# Revit family: STORA-RP 650x
name_source: partatom
category: Leuchten
units: mm (PartAtom-declared; Revit-internal decimal feet)

## family parameters
Basisbauteil = Fläche
Beim Laden mit Abzugskörper schneiden = Nein
Bemaßung runder Anschluss = Durchmesser verwenden
Gemeinsam genutzt = Nein
Lichtquelle = Ja
OmniClass-Nummer = 23.80.70.11
OmniClass-Titel = Luminaries for Internal Lighting
Raumberechnungspunkt = Nein
Teiletyp = Normal

## types (4) — shared parameters
Baugruppenkennzeichen = D5020200
Datei für fotometrisches Netz = STORA-RP_650_OS.IES
Emissionsform beim Rendern sichtbar = Nein
Farbfilter = 16777215
Farbtemperaturverschiebung bei Dämpfen der Lampe = <Keine Auswahl>
Hersteller = RIDI Leuchten GmbH
Lampe = LED
Neigungswinkel = 90.00°
Scheinlast = 37 VA
URL = www.spectral.de
Von Kreisdurchmesser aussenden = 641 mm  [stored 2.10302 ft]
Wire length = 200 mm  [stored 0.656168 ft]
brand = Spectral
conformity mark = CE
electrical safety class = 1
height = 50 mm  [stored 0.164042 ft]
ingress protection (IP) code = IP20
length = 650 mm  [stored 2.13255 ft]
nominal frequency = 50-60Hz
nominal voltage = 230
rated input power = 37
voltage type (AC, DC, UC) = AC
width = 650 mm  [stored 2.13255 ft]
zero-valued in all types: Vorgabe-Ansicht

## per-type parameters (varying)
| type | Modell | weight |
| STORA-RP 650 6000/830 OS | SPC0620064 | 5,5 kg |
| STORA-RP 650 DAFWS830OS | SPC0630064 | 7,5 kg |
| STORA-RP 650 6000/840 OS | SPC0620065 | 5,5 kg |
| STORA-RP 650 6000/840 OS-DA | SPC0630065 | 7,5 kg |

note: column(s) folded — value = type name in every type: product name

note: [stored X ft] marks values corroborated as IEEE doubles in the binary element streams (Revit-internal decimal feet)
